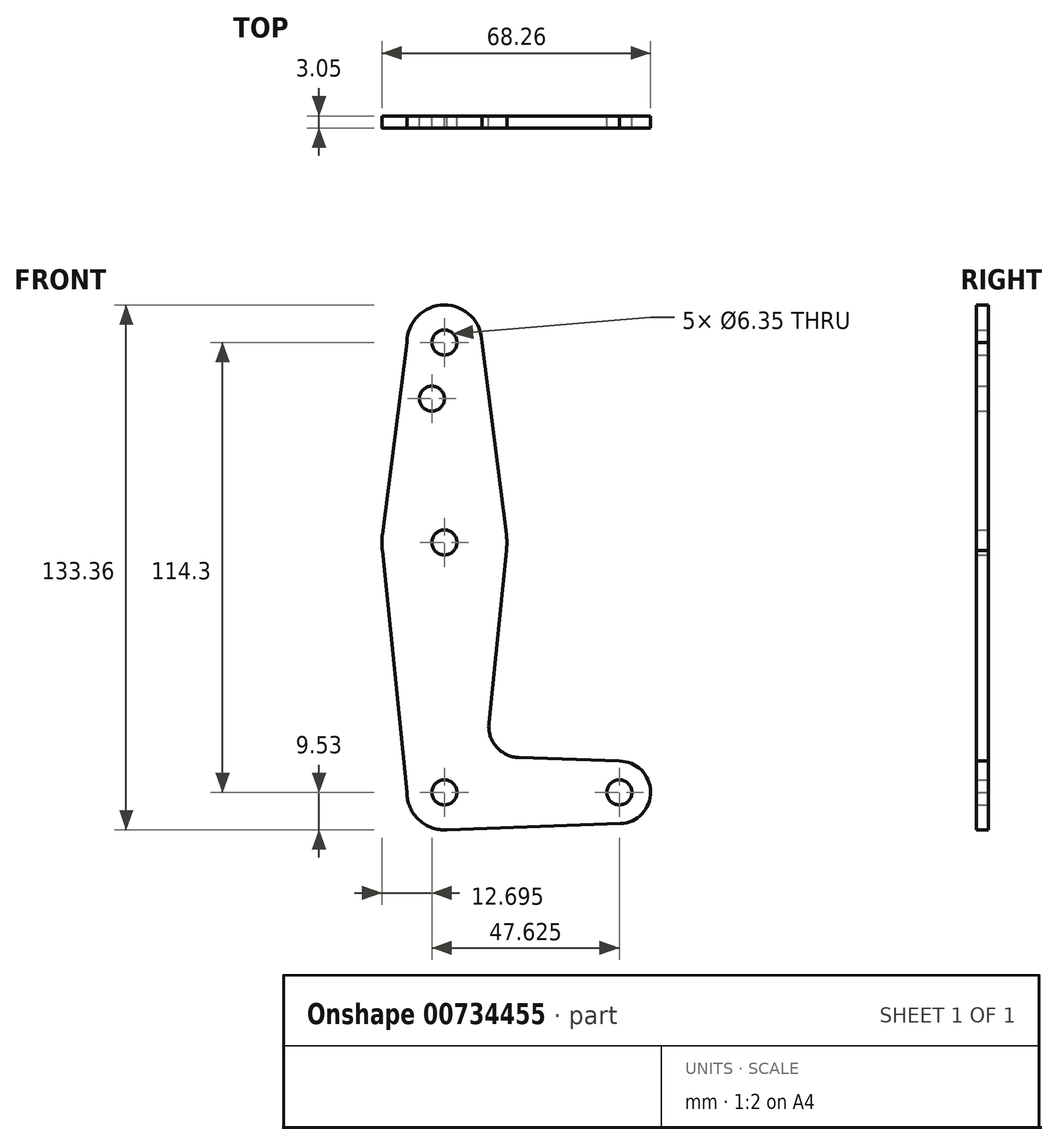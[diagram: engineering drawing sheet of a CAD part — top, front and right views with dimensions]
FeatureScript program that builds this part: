
annotation { "Feature Type Name" : "Feature", "Feature Type Description" : "" }
export const myFeature = defineFeature(function(context is Context, id is Id, definition is map)
    precondition{}
    {
        {
            var Q0;
            Q0=qCreatedBy(makeId("Front.planeOp"),FACE);
            var sketch = newSketch(context, id + "F0", { "sketchPlane" : qUnion([Q0])});
            skLineSegment(sketch, "E0", {"start": v(0, 0) * mm, "end": v(0, 114.3) * mm});
            skLineSegment(sketch, "E1", {"start": v(0, 0) * mm, "end": v(44.45, 0) * mm});
            skCircle(sketch, "E2", {"center": v(0, 114.3) * mm, "radius": 9.53 * mm});
            skCircle(sketch, "E3", {"center": v(0, 63.5) * mm, "radius": 15.88 * mm});
            skCircle(sketch, "E4", {"center": v(0, 0) * mm, "radius": 9.53 * mm});
            skCircle(sketch, "E5", {"center": v(44.45, 0) * mm, "radius": 7.94 * mm});
            skLineSegment(sketch, "E6", {"start": v(-9.52, 114.3) * mm, "end": v(-15.75, 65.5) * mm});
            skLineSegment(sketch, "E7", {"start": v(9.52, 114.3) * mm, "end": v(15.75, 65.5) * mm});
            skLineSegment(sketch, "E8", {"start": v(-15.75, 61.5) * mm, "end": v(-9.52, 0) * mm});
            skLineSegment(sketch, "E9", {"start": v(15.75, 61.5) * mm, "end": v(11.3, 17.6) * mm});
            skLineSegment(sketch, "E10", {"start": v(18.93, 8.85) * mm, "end": v(44.45, 7.94) * mm});
            skLineSegment(sketch, "E11", {"start": v(0, -9.53) * mm, "end": v(44.73, -7.93) * mm});
            skCircle(sketch, "E12", {"center": v(0, 114.3) * mm, "radius": 3.18 * mm});
            skCircle(sketch, "E13", {"center": v(0, 63.5) * mm, "radius": 3.18 * mm});
            skCircle(sketch, "E14", {"center": v(0, 0) * mm, "radius": 3.18 * mm});
            skCircle(sketch, "E15", {"center": v(44.45, 0) * mm, "radius": 3.18 * mm});
            skCircle(sketch, "E16", {"center": v(-3.18, 100.03) * mm, "radius": 3.18 * mm});
            skArc(sketch, "E17.filletArc", {"start": v(11.3, 17.6) * mm, "mid": v(13.22, 11.57) * mm, "end": v(18.93, 8.85) * mm});
            skSolve(sketch);
        }
        {
            var Q0;
            Q0 = qSketchRegion(id + "F0", true);
            var Q1;
            {var subQ0=sQuery(id+"F0.wireOp",EDGE,"E14");var subQ1=sQuery(id+"F0.wireOp",EDGE,"E0");var subQ2=makeQuery(id+"F0.imprint","INTERSECT",VERTEX,{"derivedFrom":[subQ1,subQ0]});Q1=makeQuery(id+"F0.imprint","IMPRINT",FACE,{"disambiguationData":[TD([[makeQuery(id+"F0.imprint","IMPRINT",EDGE,{"disambiguationData":[TD([[subQ2,-1.0]])],"derivedFrom":subQ1}),-1.0]])]});}
            extrude(context, id + "F1", {"entities" : qUnion([Q0, Q1]), "depth" : 3.05 * mm, "offsetDistance" : 25.4 * mm});
        }
    });
